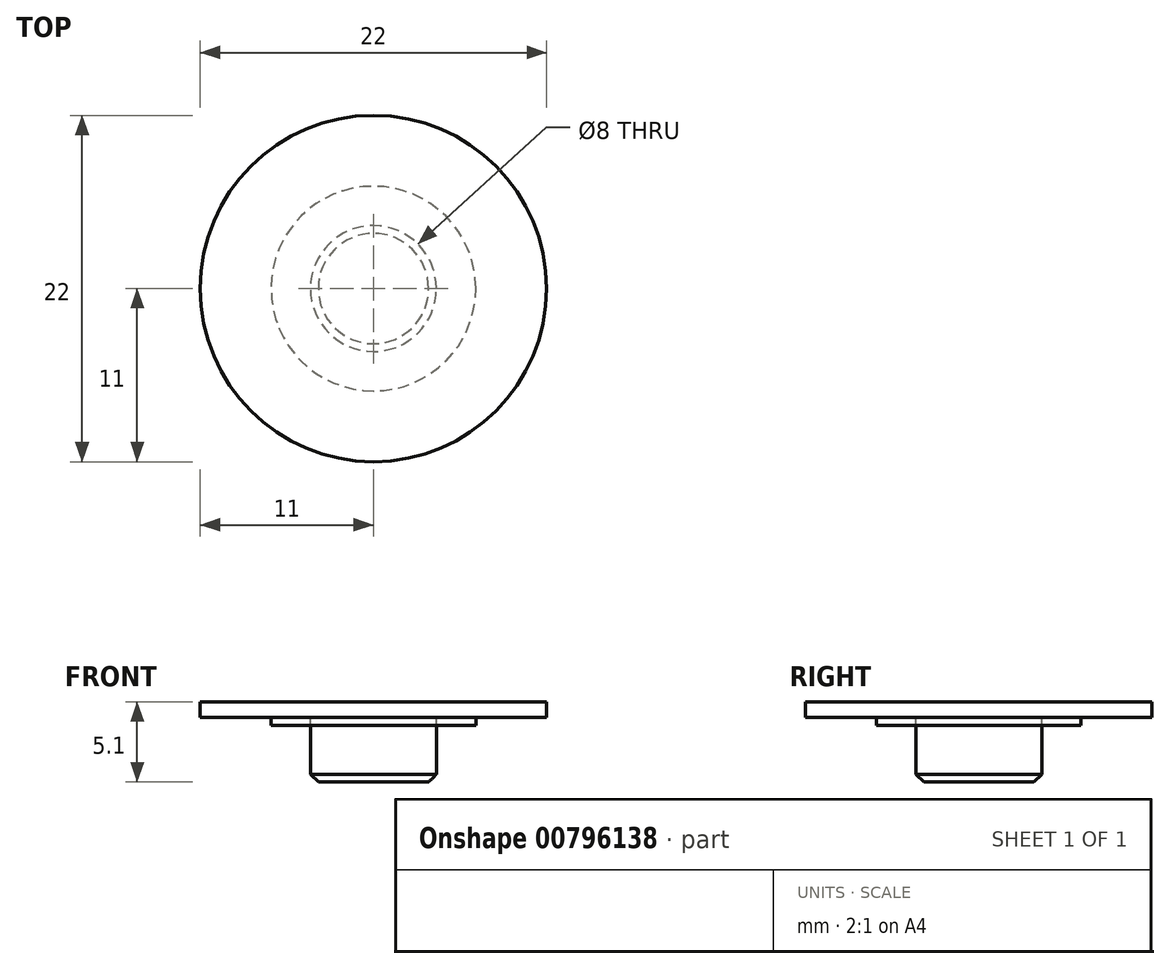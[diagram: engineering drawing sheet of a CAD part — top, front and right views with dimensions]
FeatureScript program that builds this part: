
annotation { "Feature Type Name" : "Feature", "Feature Type Description" : "" }
export const myFeature = defineFeature(function(context is Context, id is Id, definition is map)
    precondition{}
    {
        {
            var Q0;
            Q0=qCreatedBy(makeId("Top.planeOp"),FACE);
            var sketch = newSketch(context, id + "F0", { "sketchPlane" : qUnion([Q0])});
            skCircle(sketch, "E0", {"center": v(0, 0) * mm, "radius": 4 * mm});
            skCircle(sketch, "E1", {"center": v(0, 0) * mm, "radius": 6.5 * mm});
            skCircle(sketch, "E2", {"center": v(0, 0) * mm, "radius": 11 * mm});
            skSolve(sketch);
        }
        {
            var Q0;
            Q0=makeQuery(id+"F0.imprint","IMPRINT",FACE,{"disambiguationData":[TD([[makeQuery(id+"F0.imprint","IMPRINT",EDGE,{"derivedFrom":sQuery(id+"F0.wireOp",EDGE,"E0")}),1.0]])]});
            extrude(context, id + "F1", {"entities" : qUnion([Q0]), "oppositeDirection" : true, "depth" : 4.1 * mm, "offsetDistance" : 25 * mm});
        }
        {
            var Q0;
            Q0=makeQuery(id+"F0.imprint","IMPRINT",FACE,{"disambiguationData":[TD([[makeQuery(id+"F0.imprint","IMPRINT",EDGE,{"derivedFrom":sQuery(id+"F0.wireOp",EDGE,"E0")}),-1.0]])]});
            extrude(context, id + "F2", {"entities" : qUnion([Q0]), "oppositeDirection" : true, "depth" : 0.5 * mm, "offsetDistance" : 25 * mm});
        }
        {
            var Q0;
            Q0=makeQuery(id+"F0.imprint","IMPRINT",FACE,{"disambiguationData":[TD([[makeQuery(id+"F0.imprint","IMPRINT",EDGE,{"derivedFrom":sQuery(id+"F0.wireOp",EDGE,"E1")}),-1.0]])]});
            var Q1;
            Q1=makeQuery(id+"F0.imprint","IMPRINT",FACE,{"disambiguationData":[TD([[makeQuery(id+"F0.imprint","IMPRINT",EDGE,{"derivedFrom":sQuery(id+"F0.wireOp",EDGE,"E0")}),-1.0]])]});
            var Q2;
            Q2=makeQuery(id+"F0.imprint","IMPRINT",FACE,{"disambiguationData":[TD([[makeQuery(id+"F0.imprint","IMPRINT",EDGE,{"derivedFrom":sQuery(id+"F0.wireOp",EDGE,"E0")}),1.0]])]});
            extrude(context, id + "F3", {"entities" : qUnion([Q0, Q1, Q2]), "depth" : 1 * mm, "offsetDistance" : 25 * mm});
        }
        {
            var Q0;
            Q0=makeQuery(id+"F1.opExtrude","CAP_EDGE",EDGE,{"disambiguationData":[OSD([sQuery(id+"F0.wireOp",EDGE,"E0")])],"isStart":false});
            chamfer(context, id + "F4", {"entities" : qUnion([Q0]), "width" : 0.5 * mm, "tangentPropagation" : true});
        }
    });
